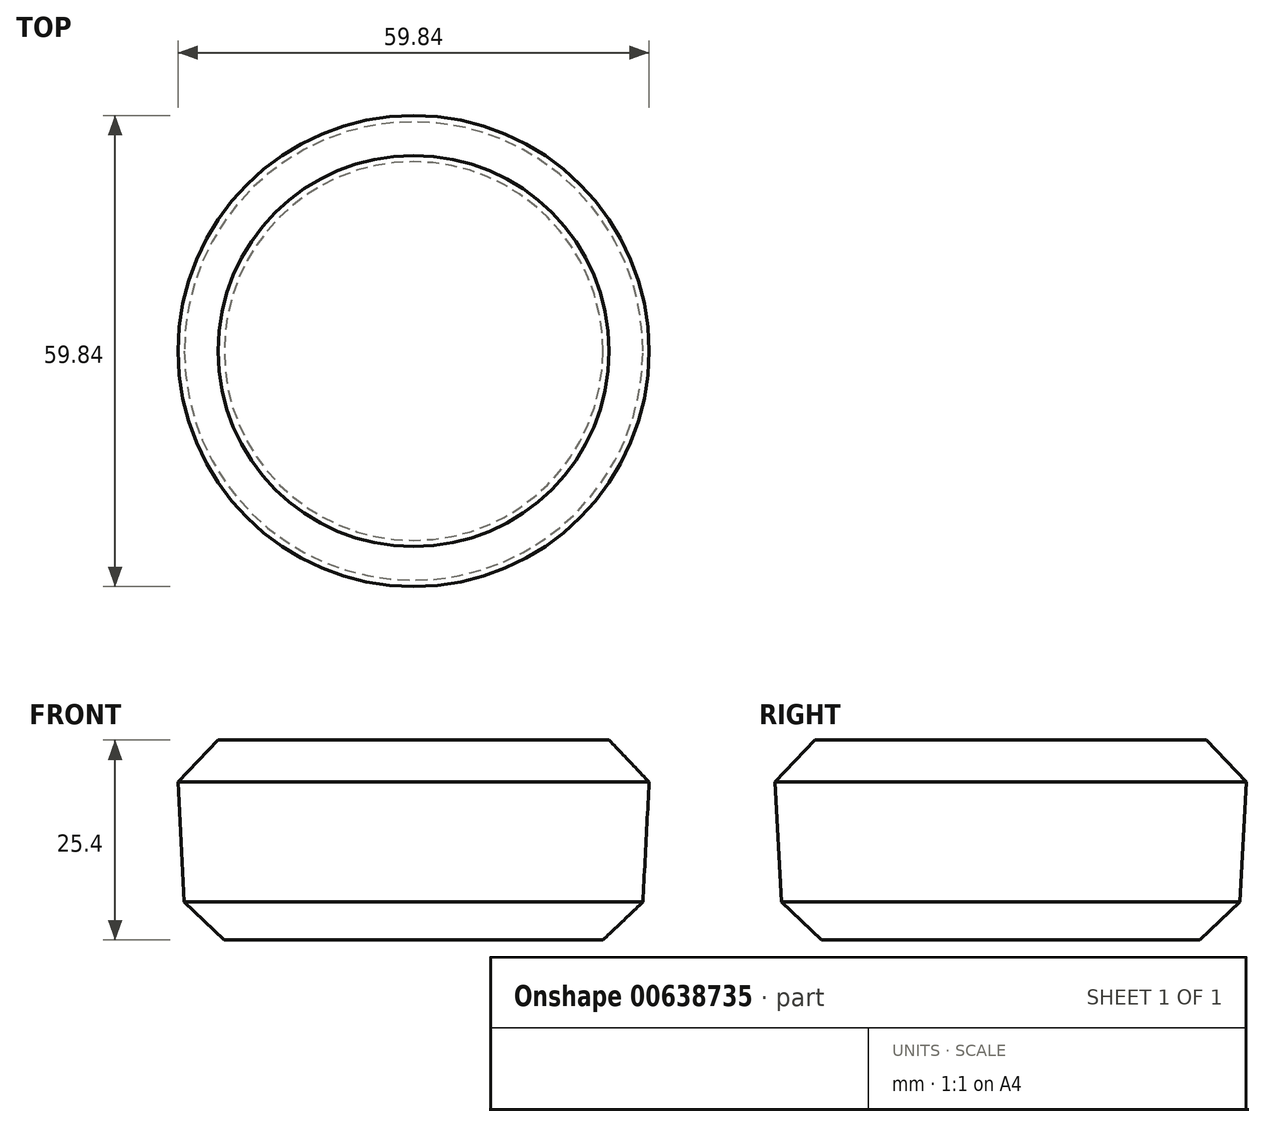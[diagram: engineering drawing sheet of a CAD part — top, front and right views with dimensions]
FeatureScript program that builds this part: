
annotation { "Feature Type Name" : "Feature", "Feature Type Description" : "" }
export const myFeature = defineFeature(function(context is Context, id is Id, definition is map)
    precondition{}
    {
        {
            var Q0;
            Q0=qCreatedBy(makeId("Top.planeOp"),FACE);
            var sketch = newSketch(context, id + "F0", { "sketchPlane" : qUnion([Q0])});
            skCircle(sketch, "E0", {"center": v(0, 0) * mm, "radius": 28.87 * mm});
            skSolve(sketch);
        }
        {
            var Q0;
            Q0 = qSketchRegion(id + "F0", true);
            extrude(context, id + "F1", {"entities" : qUnion([Q0]), "depth" : 25.4 * mm, "offsetDistance" : 25.4 * mm, "hasDraft" : true, "draftAngle" : 3 * degree});
        }
        {
            var Q0;
            Q0=makeQuery(id+"F1.opExtrude","SWEPT_FACE",FACE,{"disambiguationData":[OSD([sQuery(id+"F0.wireOp",EDGE,"E0")])]});
            chamfer(context, id + "F2", {"entities" : qUnion([Q0]), "width" : 5.08 * mm, "tangentPropagation" : true});
        }
    });
